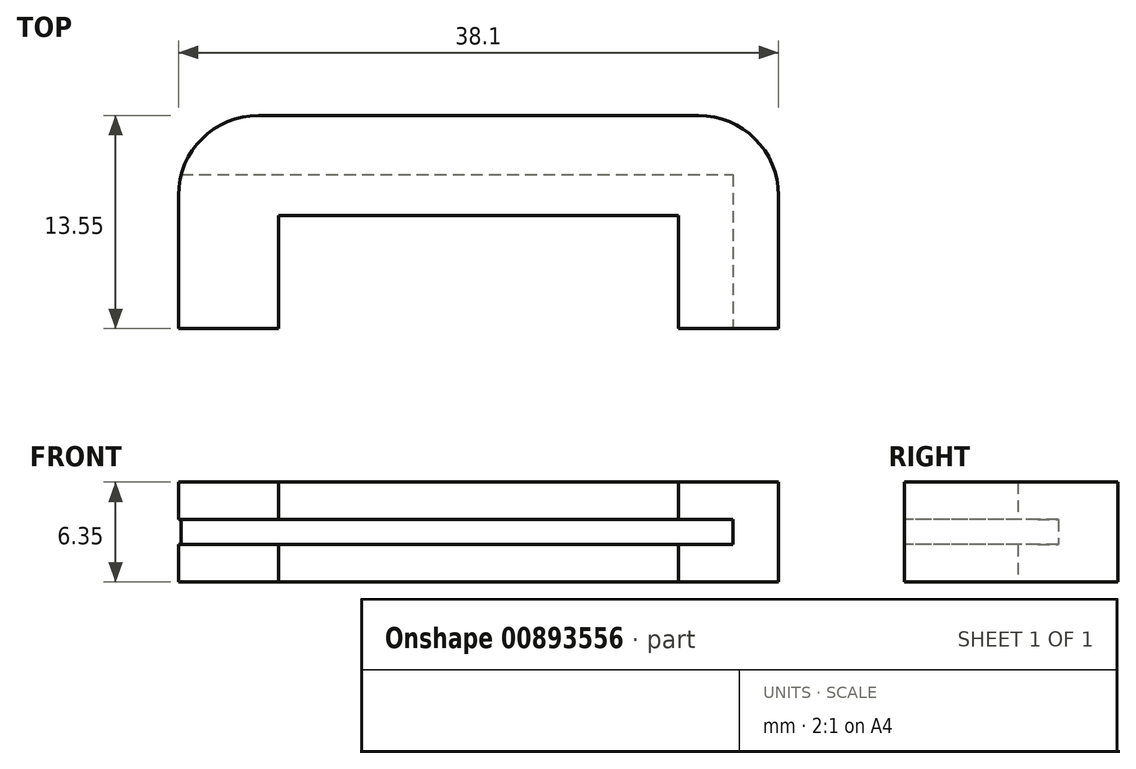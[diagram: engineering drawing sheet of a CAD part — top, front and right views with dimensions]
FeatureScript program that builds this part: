
annotation { "Feature Type Name" : "Feature", "Feature Type Description" : "" }
export const myFeature = defineFeature(function(context is Context, id is Id, definition is map)
    precondition{}
    {
        {
            var Q0;
            Q0=qCreatedBy(makeId("Top.planeOp"),FACE);
            var sketch = newSketch(context, id + "F0", { "sketchPlane" : qUnion([Q0])});
            skLineSegment(sketch, "E0", {"start": v(-19.05, 0) * mm, "end": v(-19.05, 13.55) * mm});
            skLineSegment(sketch, "E1", {"start": v(-19.05, 13.55) * mm, "end": v(19.05, 13.55) * mm});
            skLineSegment(sketch, "E2", {"start": v(19.05, 13.55) * mm, "end": v(19.05, 0) * mm});
            skLineSegment(sketch, "E3", {"start": v(-19.05, 7.2) * mm, "end": v(0, 7.2) * mm});
            skLineSegment(sketch, "E4", {"start": v(0, 7.2) * mm, "end": v(19.05, 7.2) * mm});
            skLineSegment(sketch, "E5", {"start": v(-19.05, 0) * mm, "end": v(-12.7, 0) * mm});
            skLineSegment(sketch, "E6", {"start": v(-12.7, 0) * mm, "end": v(-12.7, 13.55) * mm});
            skLineSegment(sketch, "E7", {"start": v(19.05, 0) * mm, "end": v(12.7, 0) * mm});
            skLineSegment(sketch, "E8", {"start": v(12.7, 0) * mm, "end": v(12.7, 13.55) * mm});
            skPoint(sketch, "E9", {"position": v(0, 13.55) * mm});
            skSolve(sketch);
        }
        {
            var Q0;
            {var subQ5=sQuery(id+"F0.wireOp",EDGE,"E6");var subQ6=sQuery(id+"F0.wireOp",EDGE,"E1");var subQ7=makeQuery(id+"F0.imprint","INTERSECT",VERTEX,{"derivedFrom":[subQ6,subQ5]});Q0=makeQuery(id+"F0.imprint","IMPRINT",FACE,{"disambiguationData":[TD([[makeQuery(id+"F0.imprint","IMPRINT",EDGE,{"disambiguationData":[TD([[subQ7,-1.0]])],"derivedFrom":subQ6}),-1.0]])]});}
            var Q1;
            {var subQ0=sQuery(id+"F0.wireOp",EDGE,"E1");var subQ1=sQuery(id+"F0.wireOp",EDGE,"E0");var subQ2=makeQuery(id+"F0.imprint","INTERSECT",VERTEX,{"derivedFrom":[subQ1,subQ0]});Q1=makeQuery(id+"F0.imprint","IMPRINT",FACE,{"disambiguationData":[TD([[makeQuery(id+"F0.imprint","IMPRINT",EDGE,{"disambiguationData":[TD([[subQ2,1.0]])],"derivedFrom":subQ1}),-1.0]])]});}
            var Q2;
            {var subQ0=sQuery(id+"F0.wireOp",EDGE,"E5");Q2=makeQuery(id+"F0.imprint","IMPRINT",FACE,{"disambiguationData":[TD([[makeQuery(id+"F0.imprint","IMPRINT",EDGE,{"derivedFrom":subQ0}),1.0]])]});}
            var Q3;
            {var subQ0=sQuery(id+"F0.wireOp",EDGE,"E2");var subQ1=sQuery(id+"F0.wireOp",EDGE,"E1");var subQ2=makeQuery(id+"F0.imprint","INTERSECT",VERTEX,{"derivedFrom":[subQ1,subQ0]});Q3=makeQuery(id+"F0.imprint","IMPRINT",FACE,{"disambiguationData":[TD([[makeQuery(id+"F0.imprint","IMPRINT",EDGE,{"disambiguationData":[TD([[subQ2,1.0]])],"derivedFrom":subQ1}),-1.0]])]});}
            var Q4;
            {var subQ0=sQuery(id+"F0.wireOp",EDGE,"E7");Q4=makeQuery(id+"F0.imprint","IMPRINT",FACE,{"disambiguationData":[TD([[makeQuery(id+"F0.imprint","IMPRINT",EDGE,{"derivedFrom":subQ0}),-1.0]])]});}
            extrude(context, id + "F1", {"entities" : qUnion([Q0, Q1, Q2, Q3, Q4]), "depth" : 6.35 * mm, "offsetDistance" : 25.4 * mm});
        }
        {
            var Q0;
            Q0=makeQuery(id+"F1.opExtrude","SWEPT_FACE",FACE,{"disambiguationData":[OSD([sQuery(id+"F0.wireOp",EDGE,"E5")])]});
            var sketch = newSketch(context, id + "F2", { "sketchPlane" : qUnion([Q0])});
            skLineSegment(sketch, "E10", {"start": v(-19.05, 3.97) * mm, "end": v(16.15, 3.97) * mm});
            skLineSegment(sketch, "E11", {"start": v(-19.05, 2.38) * mm, "end": v(16.18, 2.38) * mm});
            skLineSegment(sketch, "E12", {"start": v(-8.74, 6.35) * mm, "end": v(-8.74, 3.97) * mm});
            skLineSegment(sketch, "E13", {"start": v(-8.74, 2.38) * mm, "end": v(-8.74, 0) * mm});
            skLineSegment(sketch, "E14", {"start": v(9.53, 2.38) * mm, "end": v(9.53, 3.97) * mm});
            skLineSegment(sketch, "E15", {"start": v(16.15, 3.97) * mm, "end": v(16.18, 2.38) * mm});
            skSolve(sketch);
        }
        {
            var Q0;
            {var subQ0=sQuery(id+"F2.wireOp",EDGE,"E14");Q0=makeQuery(id+"F2.imprint","IMPRINT",FACE,{"disambiguationData":[TD([[makeQuery(id+"F2.imprint","IMPRINT",EDGE,{"derivedFrom":subQ0}),1.0]])]});}
            var Q1;
            {var subQ7=sQuery(id+"F2.wireOp",EDGE,"E10");var subQ9=makeQuery(id+"F2.imprint","INTERSECT",VERTEX,{"derivedFrom":[subQ7,sQuery(id+"F2.wireOp",EDGE,"E12")]});Q1=makeQuery(id+"F2.imprint","IMPRINT",FACE,{"disambiguationData":[TD([[makeQuery(id+"F2.imprint","IMPRINT",EDGE,{"disambiguationData":[TD([[subQ9,1.0]])],"derivedFrom":subQ7}),-1.0]])]});}
            extrude(context, id + "F3", {"entities" : qUnion([Q0, Q1]), "operationType" : NewBodyOperationType.REMOVE, "oppositeDirection" : true, "depth" : 9.78 * mm, "offsetDistance" : 25.4 * mm});
        }
        {
            var Q0;
            Q0=makeQuery(id+"F1.opExtrude","SWEPT_EDGE",EDGE,{"disambiguationData":[OSD([sQuery(id+"F0.wireOp",EDGE,"E1"),sQuery(id+"F0.wireOp",EDGE,"E2")])]});
            var Q1;
            Q1=makeQuery(id+"F1.opExtrude","SWEPT_EDGE",EDGE,{"disambiguationData":[OSD([sQuery(id+"F0.wireOp",EDGE,"E0"),sQuery(id+"F0.wireOp",EDGE,"E1")])]});
            fillet(context, id + "F4", {"entities" : qUnion([Q0, Q1]), "radius" : 5.08 * mm, "tangentPropagation" : true, "allowEdgeOverflow" : false});
        }
    });
